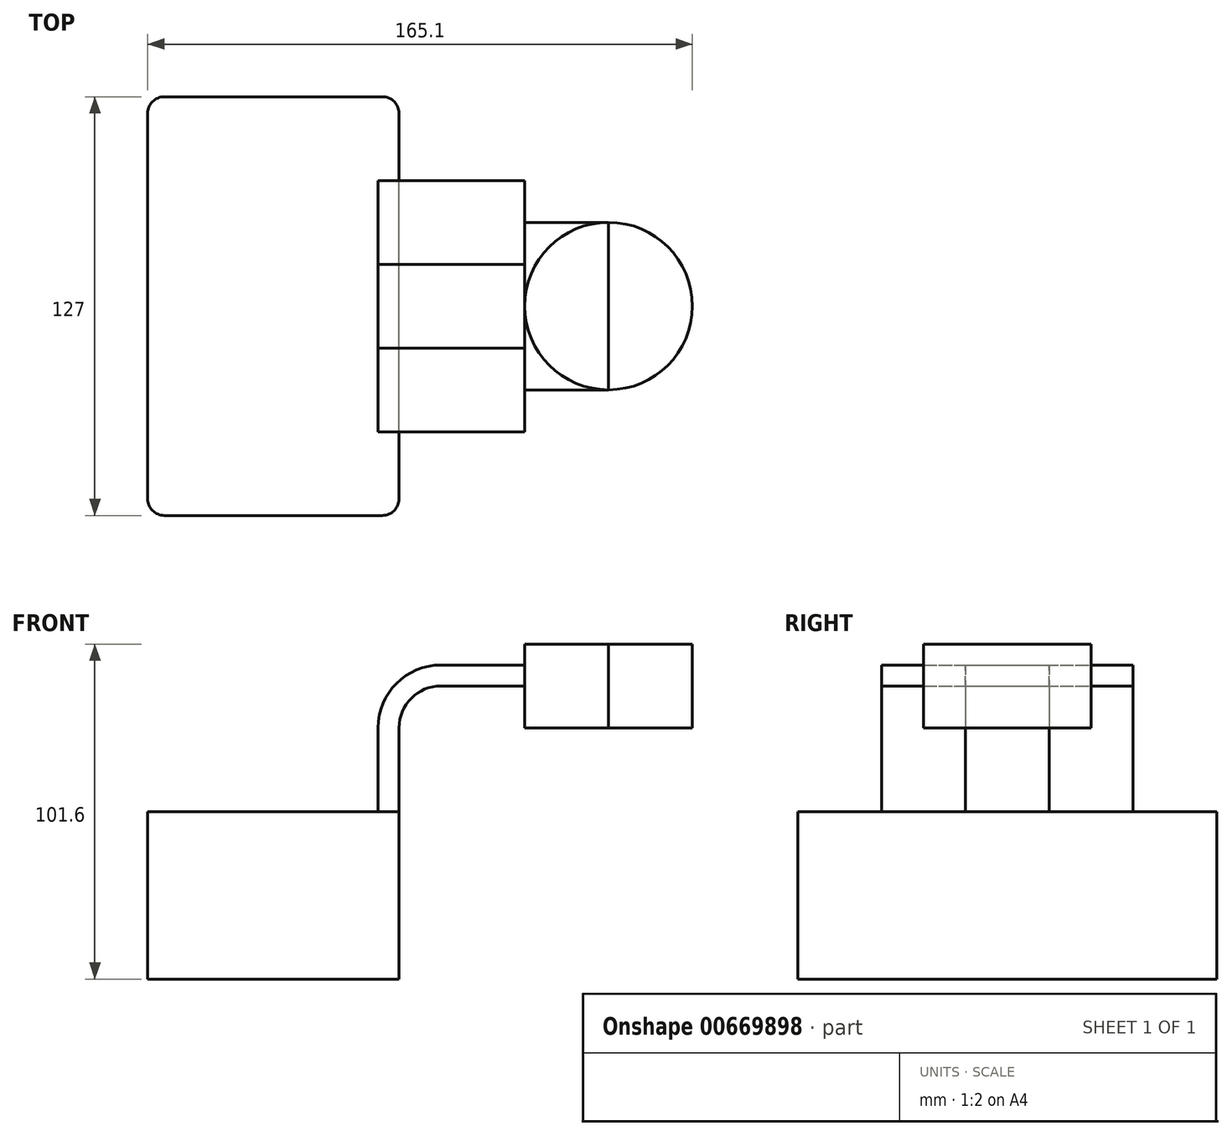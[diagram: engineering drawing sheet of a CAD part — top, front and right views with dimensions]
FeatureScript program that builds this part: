
annotation { "Feature Type Name" : "Feature", "Feature Type Description" : "" }
export const myFeature = defineFeature(function(context is Context, id is Id, definition is map)
    precondition{}
    {
        {
            var Q0;
            Q0=qCreatedBy(makeId("Front.planeOp"),FACE);
            var sketch = newSketch(context, id + "F0", { "sketchPlane" : qUnion([Q0])});
            skLineSegment(sketch, "E0.bottom", {"start": v(38.1, -25.4) * mm, "end": v(-38.1, -25.4) * mm});
            skLineSegment(sketch, "E0.top", {"start": v(38.1, 25.4) * mm, "end": v(-38.1, 25.4) * mm});
            skLineSegment(sketch, "E0.left", {"start": v(38.1, -25.4) * mm, "end": v(38.1, 25.4) * mm});
            skLineSegment(sketch, "E0.right", {"start": v(-38.1, -25.4) * mm, "end": v(-38.1, 25.4) * mm});
            skPoint(sketch, "E0.middle", {"position": v(0, 0) * mm});
            skLineSegment(sketch, "E1.bottom", {"start": v(127, 50.8) * mm, "end": v(76.2, 50.8) * mm});
            skLineSegment(sketch, "E1.top", {"start": v(127, 76.2) * mm, "end": v(76.2, 76.2) * mm});
            skLineSegment(sketch, "E1.left", {"start": v(127, 50.8) * mm, "end": v(127, 76.2) * mm});
            skLineSegment(sketch, "E1.right", {"start": v(76.2, 50.8) * mm, "end": v(76.2, 76.2) * mm});
            skPoint(sketch, "E1.middle", {"position": v(101.6, 63.5) * mm});
            skLineSegment(sketch, "E2", {"start": v(38.1, 25.4) * mm, "end": v(38.1, 50.8) * mm});
            skArc(sketch, "E3", {"start": v(38.1, 50.8) * mm, "mid": v(41.82, 59.78) * mm, "end": v(50.8, 63.5) * mm});
            skLineSegment(sketch, "E4", {"start": v(50.8, 63.5) * mm, "end": v(101.6, 63.5) * mm});
            skLineSegment(sketch, "E5.0", {"start": v(50.8, 69.85) * mm, "end": v(101.6, 69.85) * mm});
            skArc(sketch, "E5.1", {"start": v(31.75, 50.8) * mm, "mid": v(37.33, 64.27) * mm, "end": v(50.8, 69.85) * mm});
            skLineSegment(sketch, "E5.2", {"start": v(31.75, 25.4) * mm, "end": v(31.75, 50.8) * mm});
            skFitSpline(sketch, "E6", {"points": [v(-38.1, 25.4) * mm, v(-12.36, 66.45) * mm, v(76.2, 76.2) * mm], "startDerivative": vector(-92.13, 144.54) * mm, "endDerivative": vector(144.74, -3.15) * mm});
            skLineSegment(sketch, "E7", {"start": v(101.6, 63.5) * mm, "end": v(101.6, 69.85) * mm});
            skLineSegment(sketch, "E8", {"start": v(101.6, 69.85) * mm, "end": v(101.6, 76.2) * mm});
            skLineSegment(sketch, "E9", {"start": v(101.6, 63.5) * mm, "end": v(101.6, 50.8) * mm});
            skSolve(sketch);
        }
        {
            var Q0;
            Q0=makeQuery(id+"F0.imprint","IMPRINT",FACE,{"disambiguationData":[TD([[makeQuery(id+"F0.imprint","IMPRINT",EDGE,{"derivedFrom":sQuery(id+"F0.wireOp",EDGE,"E0.bottom")}),-1.0]])]});
            extrude(context, id + "F1", {"entities" : qUnion([Q0]), "endBound" : BoundingType.SYMMETRIC, "depth" : 127 * mm, "offsetDistance" : 25.4 * mm});
        }
        {
            var Q0;
            {var subQ1=sQuery(id+"F0.wireOp",EDGE,"E1.bottom");Q0=makeQuery(id+"F0.imprint","IMPRINT",FACE,{"disambiguationData":[TD([[makeQuery(id+"F0.imprint","IMPRINT",EDGE,{"derivedFrom":subQ1}),-1.0]])]});}
            var Q1;
            {var subQ5=sQuery(id+"F0.wireOp",EDGE,"E7");Q1=makeQuery(id+"F0.imprint","IMPRINT",FACE,{"disambiguationData":[TD([[makeQuery(id+"F0.imprint","IMPRINT",EDGE,{"derivedFrom":subQ5}),1.0]])]});}
            var Q2;
            {var subQ3=sQuery(id+"F0.wireOp",EDGE,"E8");Q2=makeQuery(id+"F0.imprint","IMPRINT",FACE,{"disambiguationData":[TD([[makeQuery(id+"F0.imprint","IMPRINT",EDGE,{"derivedFrom":subQ3}),1.0]])]});}
            extrude(context, id + "F2", {"entities" : qUnion([Q0, Q1, Q2]), "operationType" : NewBodyOperationType.ADD, "endBound" : BoundingType.SYMMETRIC, "depth" : 50.8 * mm, "offsetDistance" : 25.4 * mm});
        }
        {
            var Q0;
            {var subQ1=sQuery(id+"F0.wireOp",EDGE,"E2");Q0=makeQuery(id+"F0.imprint","IMPRINT",FACE,{"disambiguationData":[TD([[makeQuery(id+"F0.imprint","IMPRINT",EDGE,{"derivedFrom":subQ1}),1.0]])]});}
            extrude(context, id + "F3", {"entities" : qUnion([Q0]), "endBound" : BoundingType.SYMMETRIC, "depth" : 76.2 * mm, "offsetDistance" : 25.4 * mm});
        }
        {
            var Q0;
            {var subQ0=sQuery(id+"F0.wireOp",EDGE,"E5.1");Q0=makeQuery(id+"F0.imprint","IMPRINT",FACE,{"disambiguationData":[TD([[makeQuery(id+"F0.imprint","IMPRINT",EDGE,{"derivedFrom":subQ0}),1.0]])]});}
            extrude(context, id + "F4", {"entities" : qUnion([Q0]), "endBound" : BoundingType.SYMMETRIC, "depth" : 25.4 * mm, "offsetDistance" : 25.4 * mm});
        }
        {
            var Q0;
            {var subQ0=sQuery(id+"F0.wireOp",EDGE,"E1.left");Q0=makeQuery(id+"F0.imprint","IMPRINT",FACE,{"disambiguationData":[TD([[makeQuery(id+"F0.imprint","IMPRINT",EDGE,{"derivedFrom":subQ0}),1.0]])]});}
            var Q1;
            Q1=sQuery(id+"F0.wireOp",EDGE,"E9");
            revolve(context, id + "F5", {"entities" : qUnion([Q0]), "axis" : qUnion([Q1]), "revolveType" : RevolveType.FULL});
        }
        {
            var Q0;
            Q0=makeQuery(id+"F1.opExtrude","CAP_EDGE",EDGE,{"disambiguationData":[OSD([sQuery(id+"F0.wireOp",EDGE,"E0.left")])],"isStart":false});
            fillet(context, id + "F6", {"entities" : qUnion([Q0]), "radius" : 5.08 * mm, "tangentPropagation" : true, "allowEdgeOverflow" : false});
        }
        {
            var Q0;
            Q0=makeQuery(id+"F1.opExtrude","CAP_EDGE",EDGE,{"disambiguationData":[OSD([sQuery(id+"F0.wireOp",EDGE,"E0.right")])],"isStart":false});
            fillet(context, id + "F7", {"entities" : qUnion([Q0]), "radius" : 5.08 * mm, "tangentPropagation" : true, "allowEdgeOverflow" : false});
        }
        {
            var Q0;
            Q0=makeQuery(id+"F1.opExtrude","CAP_EDGE",EDGE,{"disambiguationData":[OSD([sQuery(id+"F0.wireOp",EDGE,"E0.right")])],"isStart":true});
            var Q1;
            Q1=makeQuery(id+"F1.opExtrude","CAP_EDGE",EDGE,{"disambiguationData":[OSD([sQuery(id+"F0.wireOp",EDGE,"E0.left")])],"isStart":true});
            fillet(context, id + "F8", {"entities" : qUnion([Q0, Q1]), "radius" : 5.08 * mm, "tangentPropagation" : true, "allowEdgeOverflow" : false});
        }
    });
